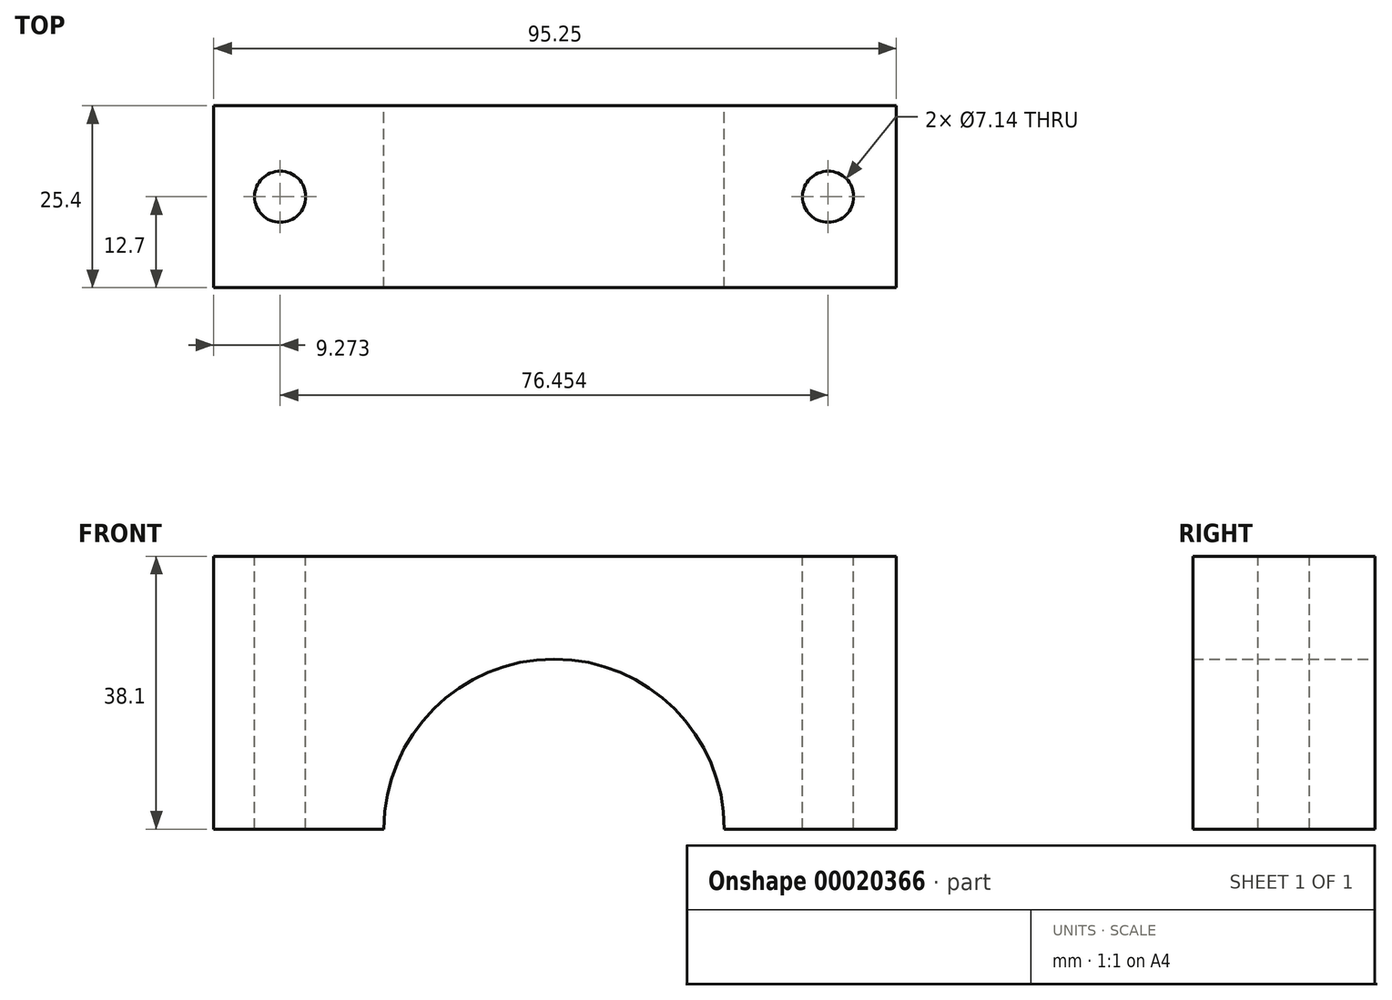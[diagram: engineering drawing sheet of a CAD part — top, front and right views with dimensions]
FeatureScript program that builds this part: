
annotation { "Feature Type Name" : "Feature", "Feature Type Description" : "" }
export const myFeature = defineFeature(function(context is Context, id is Id, definition is map)
    precondition{}
    {
        {
            var Q0;
            Q0=qCreatedBy(makeId("Front.planeOp"),FACE);
            var sketch = newSketch(context, id + "F0", { "sketchPlane" : qUnion([Q0])});
            skLineSegment(sketch, "E0.bottom", {"start": v(-57.97, 48.71) * mm, "end": v(37.28, 48.71) * mm});
            skLineSegment(sketch, "E0.left", {"start": v(-57.97, 48.71) * mm, "end": v(-57.97, 10.61) * mm});
            skLineSegment(sketch, "E0.right", {"start": v(37.28, 48.71) * mm, "end": v(37.28, 10.61) * mm});
            skArc(sketch, "E1", {"start": v(13.28, 10.61) * mm, "mid": v(-10.47, 34.36) * mm, "end": v(-34.22, 10.61) * mm});
            skLineSegment(sketch, "E2", {"start": v(-57.97, 10.61) * mm, "end": v(-34.22, 10.61) * mm});
            skLineSegment(sketch, "E3.trimOffspring", {"start": v(13.28, 10.61) * mm, "end": v(37.28, 10.61) * mm});
            skSolve(sketch);
        }
        {
            var Q0;
            Q0 = qSketchRegion(id + "F0", true);
            extrude(context, id + "F1", {"entities" : qUnion([Q0]), "depth" : 25.4 * mm});
        }
        {
            var Q0;
            Q0=makeQuery(id+"F1.opExtrude","SWEPT_FACE",FACE,{"disambiguationData":[OSD([sQuery(id+"F0.wireOp",EDGE,"E0.bottom")])]});
            var sketch = newSketch(context, id + "F2", { "sketchPlane" : qUnion([Q0])});
            skLineSegment(sketch, "E4.0", {"start": v(27.76, -25.4) * mm, "end": v(27.76, 0) * mm, "construction": true});
            skLineSegment(sketch, "E5.0", {"start": v(-57.97, -12.7) * mm, "end": v(37.28, -12.7) * mm, "construction": true});
            skLineSegment(sketch, "E6.0", {"start": v(-10.47, -25.4) * mm, "end": v(-10.47, 0) * mm, "construction": true});
            skCircle(sketch, "E7", {"center": v(27.76, -12.7) * mm, "radius": 3.57 * mm});
            skCircle(sketch, "E8.MirrorC", {"center": v(-48.7, -12.7) * mm, "radius": 3.57 * mm});
            skSolve(sketch);
        }
        {
            var Q0;
            Q0 = qSketchRegion(id + "F2", true);
            extrude(context, id + "F3", {"entities" : qUnion([Q0]), "operationType" : NewBodyOperationType.REMOVE, "endBound" : BoundingType.THROUGH_ALL, "oppositeDirection" : true, "depth" : 25.4 * mm});
        }
    });
